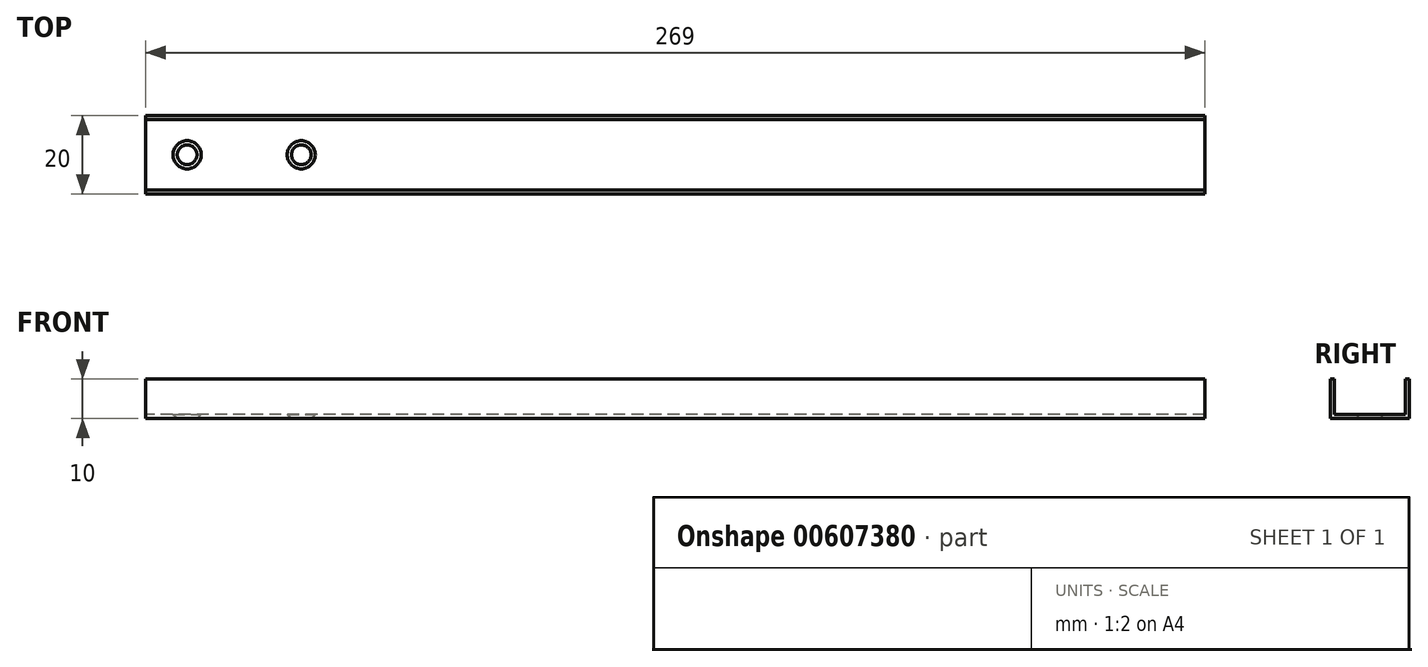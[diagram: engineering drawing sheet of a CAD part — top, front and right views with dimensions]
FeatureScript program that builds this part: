
annotation { "Feature Type Name" : "Feature", "Feature Type Description" : "" }
export const myFeature = defineFeature(function(context is Context, id is Id, definition is map)
    precondition{}
    {
        {
            var Q0;
            Q0=qCreatedBy(makeId("Right.planeOp"),FACE);
            var sketch = newSketch(context, id + "F0", { "sketchPlane" : qUnion([Q0])});
            skLineSegment(sketch, "E0.bottom", {"start": v(10, -5) * mm, "end": v(-10, -5) * mm});
            skLineSegment(sketch, "E0.top", {"start": v(10, 5) * mm, "end": v(-10, 5) * mm});
            skLineSegment(sketch, "E0.left", {"start": v(10, -5) * mm, "end": v(10, 5) * mm});
            skLineSegment(sketch, "E0.right", {"start": v(-10, -5) * mm, "end": v(-10, 5) * mm});
            skPoint(sketch, "E0.middle", {"position": v(0, 0) * mm});
            skLineSegment(sketch, "E1.bottom", {"start": v(9, 5) * mm, "end": v(-9, 5) * mm});
            skLineSegment(sketch, "E1.top", {"start": v(9, -4) * mm, "end": v(-9, -4) * mm});
            skLineSegment(sketch, "E1.left", {"start": v(9, 5) * mm, "end": v(9, -4) * mm});
            skLineSegment(sketch, "E1.right", {"start": v(-9, 5) * mm, "end": v(-9, -4) * mm});
            skSolve(sketch);
        }
        {
            var Q0;
            Q0=makeQuery(id+"F0.imprint","IMPRINT",FACE,{"disambiguationData":[TD([[makeQuery(id+"F0.imprint","IMPRINT",EDGE,{"derivedFrom":sQuery(id+"F0.wireOp",EDGE,"E0.bottom")}),-1.0]])]});
            extrude(context, id + "F1", {"entities" : qUnion([Q0]), "depth" : 134.5 * mm, "offsetDistance" : 25 * mm, "hasSecondDirection" : true, "secondDirectionOppositeDirection" : true, "secondDirectionDepth" : 134.5 * mm});
        }
        {
            var Q0;
            Q0=makeQuery(id+"F1.opExtrude","SWEPT_FACE",FACE,{"disambiguationData":[OSD([sQuery(id+"F0.wireOp",EDGE,"E0.bottom")])]});
            var sketch = newSketch(context, id + "F2", { "sketchPlane" : qUnion([Q0])});
            skLineSegment(sketch, "E2", {"start": v(-134.5, 0) * mm, "end": v(134.5, 0) * mm, "construction": true});
            skCircle(sketch, "E3", {"center": v(-124, 0) * mm, "radius": 2.5 * mm});
            skCircle(sketch, "E4", {"center": v(-95, 0) * mm, "radius": 2.5 * mm});
            skLineSegment(sketch, "E5", {"start": v(0, -23.81) * mm, "end": v(-5.5, -23.81) * mm, "construction": true});
            skLineSegment(sketch, "E6", {"start": v(0, -26.52) * mm, "end": v(-3, -26.52) * mm, "construction": true});
            skLineSegment(sketch, "E7", {"start": v(-3, -26.52) * mm, "end": v(-5.5, -23.81) * mm, "construction": true});
            skSolve(sketch);
        }
        {
            var Q0;
            Q0 = qSketchRegion(id + "F2", true);
            extrude(context, id + "F3", {"entities" : qUnion([Q0]), "operationType" : NewBodyOperationType.REMOVE, "oppositeDirection" : true, "depth" : 1 * mm, "offsetDistance" : 25 * mm, "hasDraft" : true, "draftAngle" : 0.83 * radian});
        }
    });
